# Revit family: PV_Compact_DN015_5-30_MM_RFA_2018
name_source: partatom
category: Pipe Accessories
revit_build: Autodesk Revit LT 2018 (Build: 20180329_1100(x64)
units: mm (PartAtom-declared; Revit-internal decimal feet)

## family parameters
Always vertical = Yes
Cut with Voids When Loaded = No
Part Type = Valve - Breaks Into
Round Connector Dimension = Use Diameter
Shared = No
Work Plane-Based = No

## types (2) — shared parameters
CAT0 = Yes
D = 15 mm
Description = Nastavitelný regulátor tlakové diference
L2D = 65 mm
L2D_Min = 30 mm  [stored 0.0984252 ft]
LM = 45 mm  [stored 0.147638 ft]
M2 = 23 mm
M3 = 25 mm  [stored 0.082021 ft]
M4 = 31 mm
M5 = 33 mm  [stored 0.108268 ft]
MC Pressure Drop Maximum Value = 0.0 Pa
MC Pressure Drop Minimum Value = 0.0 Pa
MC Use Limits From Balancing Method = No
Manufacturer = Hydronic Systems Prague s.r.o.
QmdConnectorList = 301;D;302;D
R1 = 19 mm  [stored 0.062336 ft]
R2 = 11 mm  [stored 0.0360892 ft]
R3 = 10 mm  [stored 0.0328084 ft]
R4 = 15 mm  [stored 0.0492126 ft]
R5 = 5 mm  [stored 0.0164042 ft]
R6 = 13 mm  [stored 0.0426509 ft]
Type Comments = závitový s vnějším závitem; PN25; dpmax=450kPa; -10~+120°C;
URL = www.hydronic.cz
W2D = 15 mm  [stored 0.0492126 ft]
XR1 = 13 mm  [stored 0.0426509 ft]
XR2 = 25 mm  [stored 0.082021 ft]
XR3 = 30 mm  [stored 0.0984252 ft]
Z2 = 33 mm  [stored 0.108268 ft]
Z3 = 6 mm  [stored 0.019685 ft]
Z4 = 39 mm  [stored 0.127953 ft]
Z5 = 44 mm  [stored 0.144357 ft]
Z6 = 40 mm  [stored 0.131234 ft]
Z7 = 15 mm  [stored 0.0492126 ft]
magiPartTypeId = 304
magiProductFamilyId = Frese PV Compact *
zero-valued in all types: MC Throttling Maximum Value, MC Throttling Minimum Value

## per-type parameters (varying)
| type | MC Product Code | magiProductId |
| PV Compact DN15 MM (20-60 kPa) | 53-3201 DN15; MM; nastavitelný rozsah dp=20~60kPa; Q=100~1000l/h;  kvs=2,9 | Frese PV Compact DN15-2 |
| Frese PV Compact DN15 MM (5-30 kPa) | 53-3200 DN15; MM; nastavitelný rozsah dp=5~30kPa; Q=50~600l/h;  kvs=2,9 | Frese PV Compact DN15-1 |

note: [stored X ft] marks values corroborated as IEEE doubles in the binary element streams (Revit-internal decimal feet)

## geometry (parser evidence)
native form markers: Sweep x2
no freeform markers — native parametric forms only
